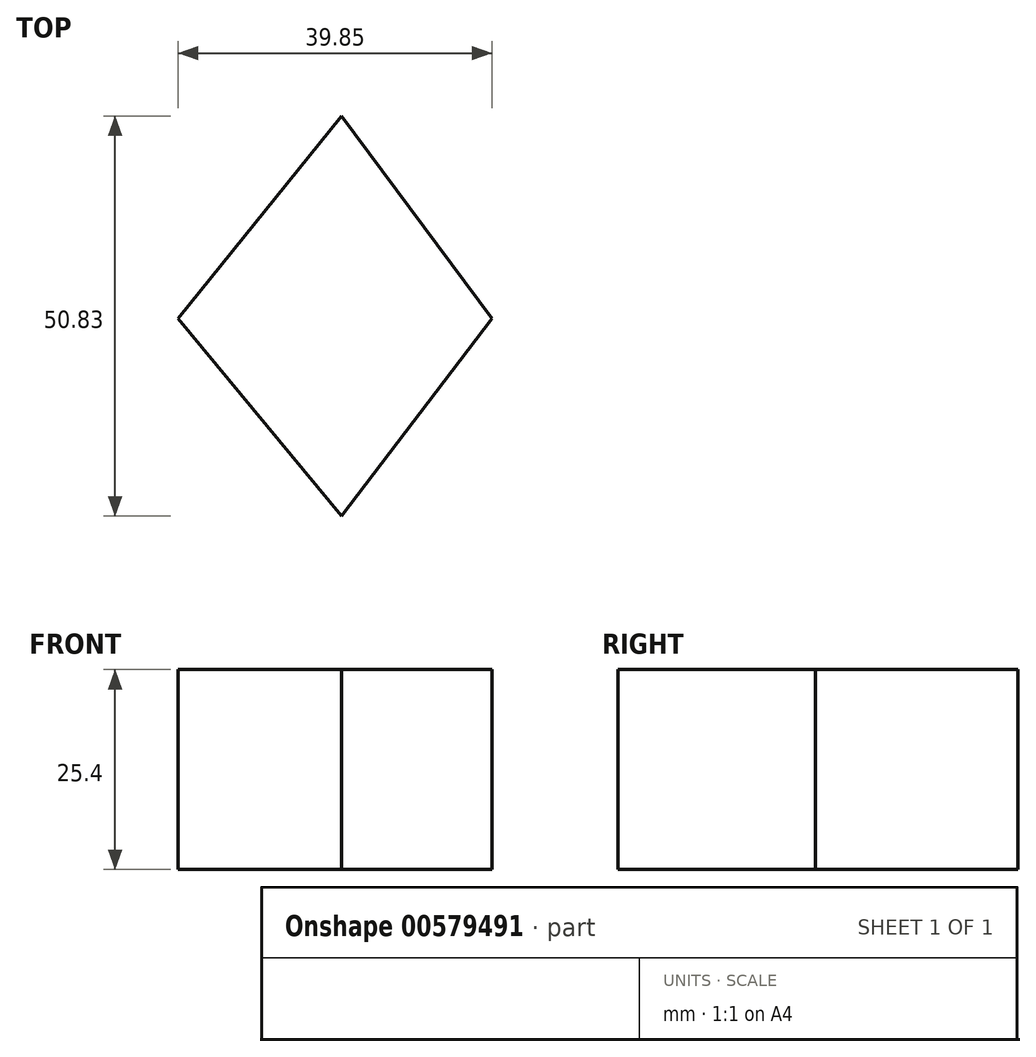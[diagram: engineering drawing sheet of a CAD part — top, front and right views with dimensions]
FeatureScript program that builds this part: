
annotation { "Feature Type Name" : "Feature", "Feature Type Description" : "" }
export const myFeature = defineFeature(function(context is Context, id is Id, definition is map)
    precondition{}
    {
        {
            var Q0;
            Q0=qCreatedBy(makeId("Top.planeOp"),FACE);
            var sketch = newSketch(context, id + "F0", { "sketchPlane" : qUnion([Q0])});
            skLineSegment(sketch, "E0", {"start": v(-20.78, 14.58) * mm, "end": v(0, 40.32) * mm});
            skLineSegment(sketch, "E1", {"start": v(-20.78, 14.58) * mm, "end": v(19.07, 14.58) * mm});
            skLineSegment(sketch, "E2", {"start": v(0, 40.32) * mm, "end": v(19.07, 14.58) * mm});
            skLineSegment(sketch, "E3", {"start": v(-20.78, 14.58) * mm, "end": v(0, -10.5) * mm});
            skLineSegment(sketch, "E4", {"start": v(19.07, 14.58) * mm, "end": v(0, -10.5) * mm});
            skSolve(sketch);
        }
        {
            var Q0;
            Q0=makeQuery(id+"F0.imprint","IMPRINT",FACE,{"disambiguationData":[TD([[makeQuery(id+"F0.imprint","IMPRINT",EDGE,{"derivedFrom":sQuery(id+"F0.wireOp",EDGE,"E0")}),-1.0]])]});
            var Q1;
            Q1=makeQuery(id+"F0.imprint","IMPRINT",FACE,{"disambiguationData":[TD([[makeQuery(id+"F0.imprint","IMPRINT",EDGE,{"derivedFrom":sQuery(id+"F0.wireOp",EDGE,"E1")}),-1.0]])]});
            extrude(context, id + "F1", {"entities" : qUnion([Q0, Q1]), "depth" : 25.4 * mm, "offsetDistance" : 25.4 * mm});
        }
    });
